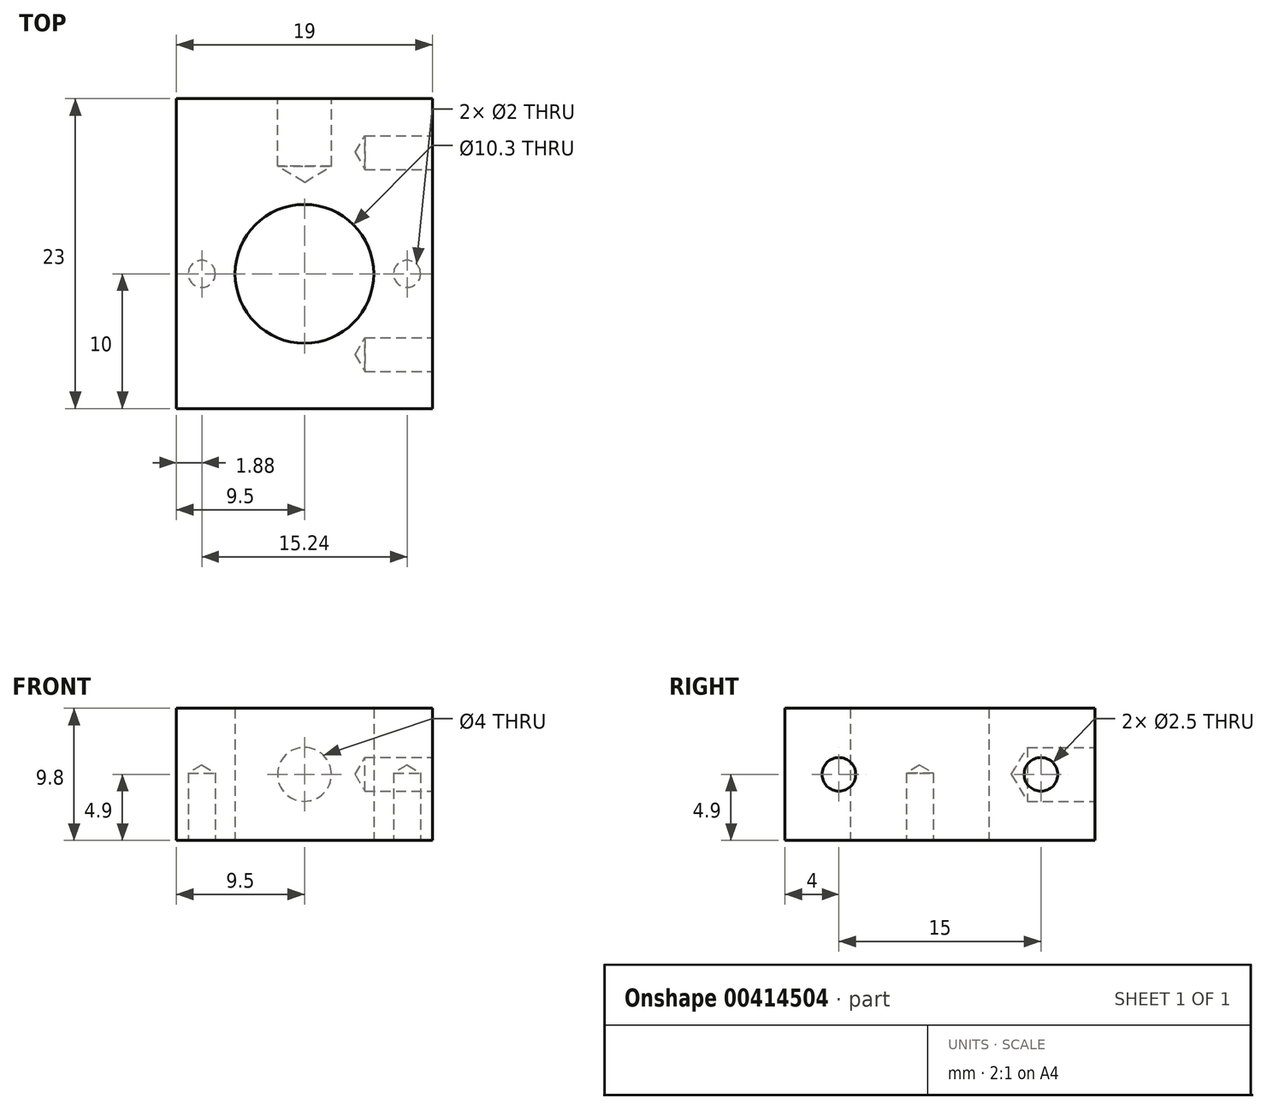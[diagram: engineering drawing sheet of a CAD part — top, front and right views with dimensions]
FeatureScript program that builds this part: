
annotation { "Feature Type Name" : "Feature", "Feature Type Description" : "" }
export const myFeature = defineFeature(function(context is Context, id is Id, definition is map)
    precondition{}
    {
        {
            var Q0;
            Q0=qCreatedBy(makeId("Top.planeOp"),FACE);
            var sketch = newSketch(context, id + "F0", { "sketchPlane" : qUnion([Q0])});
            skLineSegment(sketch, "E0.top", {"start": v(-9.5, -10) * mm, "end": v(9.5, -10) * mm});
            skLineSegment(sketch, "E0.left", {"start": v(-9.5, 13) * mm, "end": v(-9.5, -10) * mm});
            skCircle(sketch, "E1", {"center": v(0, 0) * mm, "radius": 5.15 * mm});
            skLineSegment(sketch, "E2", {"start": v(9.5, -10) * mm, "end": v(9.5, 13) * mm});
            skLineSegment(sketch, "E3", {"start": v(-9.5, 13) * mm, "end": v(9.5, 13) * mm});
            skSolve(sketch);
        }
        {
            var Q0;
            Q0=makeQuery(id+"F0.imprint","IMPRINT",FACE,{"disambiguationData":[TD([[makeQuery(id+"F0.imprint","IMPRINT",EDGE,{"derivedFrom":sQuery(id+"F0.wireOp",EDGE,"E0.top")}),1.0]])]});
            extrude(context, id + "F1", {"entities" : qUnion([Q0]), "depth" : 9.8 * mm});
        }
        {
            var Q0;
            Q0=makeQuery(id+"F1.opExtrude","CAP_FACE",FACE,{"disambiguationData":[OSD([sQuery(id+"F0.wireOp",EDGE,"E0.bottom"),sQuery(id+"F0.wireOp",EDGE,"E0.top"),sQuery(id+"F0.wireOp",EDGE,"E0.left"),sQuery(id+"F0.wireOp",EDGE,"E0.right"),sQuery(id+"F0.wireOp",EDGE,"E1")])],"isStart":true});
            var sketch = newSketch(context, id + "F2", { "sketchPlane" : qUnion([Q0])});
            skLineSegment(sketch, "E4", {"start": v(-7.62, 0) * mm, "end": v(7.62, 0) * mm, "construction": true});
            skSolve(sketch);
        }
        {
            var Q0;
            Q0=sQuery(id+"F2.wireOp",VERTEX,"E4.start");
            var Q1;
            Q1=sQuery(id+"F2.wireOp",VERTEX,"E4.end");
            var Q2;
            Q2=makeQuery(id+"F1.opExtrude","SWEPT_BODY",BODY,{"disambiguationData":[OSD([sQuery(id+"F0.wireOp",EDGE,"E0.bottom"),sQuery(id+"F0.wireOp",EDGE,"E0.top"),sQuery(id+"F0.wireOp",EDGE,"E0.left"),sQuery(id+"F0.wireOp",EDGE,"E0.right"),sQuery(id+"F0.wireOp",EDGE,"E1")])]});
            hole(context, id + "F3", {"style" : HoleStyle.SIMPLE, "endStyle" : HoleEndStyle.BLIND, "holeDiameter" : 2 * mm, "holeDepth" : 5 * mm, "tappedDepth" : 5 * mm, "tapClearance" : 2, "startFromSketch" : true, "locations" : qUnion([Q0, Q1]), "scope" : qUnion([Q2])});
        }
        {
            var Q0;
            Q0=makeQuery(id+"F1.opExtrude","SWEPT_FACE",FACE,{"disambiguationData":[OSD([sQuery(id+"F0.wireOp",EDGE,"E3")])]});
            var sketch = newSketch(context, id + "F4", { "sketchPlane" : qUnion([Q0])});
            skPoint(sketch, "E5", {"position": v(0, 4.9) * mm});
            skSolve(sketch);
        }
        {
            var Q0;
            Q0=sQuery(id+"F4.wireOp",VERTEX,"E5");
            var Q1;
            Q1=makeQuery(id+"F1.opExtrude","SWEPT_BODY",BODY,{"disambiguationData":[OSD([sQuery(id+"F0.wireOp",EDGE,"E0.top"),sQuery(id+"F0.wireOp",EDGE,"E0.left"),sQuery(id+"F0.wireOp",EDGE,"E1"),sQuery(id+"F0.wireOp",EDGE,"E2"),sQuery(id+"F0.wireOp",EDGE,"E3")])]});
            hole(context, id + "F5", {"style" : HoleStyle.SIMPLE, "endStyle" : HoleEndStyle.BLIND, "standardTappedOrClearance" : lookupTablePath({ "standard" : "ISO", "size" : "4", "type" : "Drilled" }), "standardBlindInLast" : lookupTablePath({ "standard" : "ISO", "size" : "4", "type" : "Drilled" }), "holeDiameter" : 4 * mm, "holeDepth" : 5 * mm, "tappedDepth" : 5 * mm, "tapClearance" : 2, "startFromSketch" : true, "locations" : qUnion([Q0]), "scope" : qUnion([Q1])});
        }
        {
            var Q0;
            Q0=makeQuery(id+"F1.opExtrude","SWEPT_FACE",FACE,{"disambiguationData":[OSD([sQuery(id+"F0.wireOp",EDGE,"E2")])]});
            var sketch = newSketch(context, id + "F6", { "sketchPlane" : qUnion([Q0])});
            skLineSegment(sketch, "E6", {"start": v(-6, 4.9) * mm, "end": v(9, 4.9) * mm, "construction": true});
            skSolve(sketch);
        }
        {
            var Q0;
            Q0=sQuery(id+"F6.wireOp",VERTEX,"E6.start");
            var Q1;
            Q1=sQuery(id+"F6.wireOp",VERTEX,"E6.end");
            var Q2;
            Q2=makeQuery(id+"F1.opExtrude","SWEPT_BODY",BODY,{"disambiguationData":[OSD([sQuery(id+"F0.wireOp",EDGE,"E0.top"),sQuery(id+"F0.wireOp",EDGE,"E0.left"),sQuery(id+"F0.wireOp",EDGE,"E1"),sQuery(id+"F0.wireOp",EDGE,"E2"),sQuery(id+"F0.wireOp",EDGE,"E3")])]});
            hole(context, id + "F7", {"style" : HoleStyle.SIMPLE, "endStyle" : HoleEndStyle.BLIND, "standardTappedOrClearance" : lookupTablePath({ "standard" : "ISO", "engagement" : "75%", "pitch" : "0.5 mm", "size" : "M3", "type" : "Tapped" }), "standardBlindInLast" : lookupTablePath({ "standard" : "ISO", "engagement" : "75%", "pitch" : "0.5 mm", "size" : "M3", "type" : "Tapped" }), "holeDiameter" : 2.5 * mm, "showTappedDepth" : true, "holeDepth" : 5 * mm, "tappedDepth" : 4 * mm, "tapClearance" : 2, "startFromSketch" : true, "locations" : qUnion([Q0, Q1]), "scope" : qUnion([Q2]), "majorDiameter" : 3 * mm});
        }
    });
